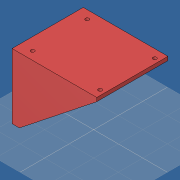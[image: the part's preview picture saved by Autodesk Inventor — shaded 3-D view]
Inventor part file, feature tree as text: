
AUTODESK INVENTOR PART (.ipt)
format: ipt  version: 2019 (Build 230136000, 136)  size: 180,736 bytes
history: native  units: mm
features: extrude x7, sketch x5
ambient origin geometry x8: Origin, YZ Plane, XZ Plane, XY Plane, X Axis, Y Axis, Z Axis, Center Point
bodies: Volumenkörper1 (feature_tree)
feature tree (12):
  sketch  "Skizze1"  dims[d0=63.0mm d1=52.0mm]
  extrude  "Extrusion1"  Depth=52.0mm
  extrude  "Extrusion2"  Depth=3.0mm
  sketch  "Skizze2"  dims[d4=3.0mm d9=44.5mm]
  extrude  "Extrusion4"  Depth=6.0mm
  extrude  "Extrusion3"  Depth=50.0mm TaperAngle=0.0deg
  extrude  "Extrusion5"  Depth=37.0mm
  extrude  "Extrusion6"  Depth=5.5mm
  extrude  "Extrusion7"  Depth=3.0mm TaperAngle=0.0deg
  sketch  "Skizze3"  dims[d10=55.0mm d11=6.0mm]
  sketch  "Skizze4"  dims[d12=3.0mm d13=0.0mm d14=50.0mm d15=0.0mm]
  sketch  "Skizze5"  dims[d30=37.0mm d31=37.0mm d39=5.5mm d40=3.0mm d41=0.0mm d42=3.5mm d43=3.0mm d44=0.0mm d45=8.0mm d47=3.0mm d48=0.0mm d49=3.0mm d50=0.0mm d51=15.0mm d52=3.0mm d53=0.0mm]
